# Revit family: 15_CMP_FD312_PB2A
name_source: partatom
category: Porte
units: mm (PartAtom-declared; Revit-internal decimal feet)

## family parameters
Condiviso = No
Host = Muro
Numero OmniClass = 23.30.10.00
Punto di calcolo locali = Sì
Sempre verticale = Sì
Taglio con vuoti quando caricato = No
Titolo OmniClass = Doors

## types (3) — shared parameters
Altezza = 2100 mm
Chiusura muro = Per host
Codice assieme = B2030100
Costruzione analitica = <Nessuno>
EXTERNAL ALUMINUM FRAME/TELAIO ALLUMINIO ESTERNO = UNIFORM_ALUMINUM
Funzione = Interno
H = 2100 mm
HANDLE HEIGHT/ALTEZZA MANIGLIA = 1100 mm  [stored 3.60892 ft]
HANDLE/MANIGLIA = UNIFORM_ALUMINUM
HOLE_H = 2100 mm
HTI = 2085 mm  [stored 6.84055 ft]
INTERIOR WOOD FRAME/TELAIO LEGNO INTERNO = UNIFORM_WOOD
Immagine tipo = <Nessuno>
Larghezza telaio = 75 mm  [stored 0.246063 ft]
MAXIMUM WIDTH/LARGHEZZA MASSIMA = 1800 mm  [stored 5.90551 ft]
MAX_DIMENSIONS_WARNING = No
MINIMUM HEIGHT/ALTEZZA MINIMA = 1800 mm  [stored 5.90551 ft]
MINIMUM WIDTH/LARGHEZZA MINIMA  = 900 mm  [stored 2.95276 ft]
Modello = COMPLANARE
PRODUCER WEBSITE/SITO WEB PRODUTTORE = www.uniform.it
PRODUCT WEBSITE/SITO WEB PRODOTTO = www.sistema-uni-one.it
Produttore = UNIFORM
Proiezione telaio est. = 25 mm  [stored 0.082021 ft]
Proiezione telaio int. = 25 mm  [stored 0.082021 ft]
URL = https://www.sistema-uni-one.it
WINDOW GLASS/VETRO FINESTRA = UNIFORM_GLASS
zero-valued in all types: T_F_H, WINDOW HOLE TOLERANCE/TOLLERANZA FORO FINESTRA

## per-type parameters (varying)
| type | GLASS WEIGHT/PESO VETRO | HOLE_W | Larghezza | MAXIMUM HEIGHT/ALTEZZA MASSIMA | Rw GLASS/Rw VETRO | Rw WINDOW/Rw FINESTRA | Ug GLASS/Ug VETRO | Uw WINDOW/Uw FINESTRA | W | W/2 | W/2 APR |
| PB2A_ACOUSTICS | 60.00 kg/m² | 1800 mm  [stored 5.90551 ft] | 1800 mm  [stored 5.90551 ft] | 2400 mm | 49 | 43 | 1.1000 W/(m²·K) | 1.3000 W/(m²·K) | 1800 mm  [stored 5.90551 ft] | 932 mm | 931 mm  [stored 3.05446 ft] |
| PB2A_THERMAL | 43.00 kg/m² | 1000 mm  [stored 3.28084 ft] | 1000 mm  [stored 3.28084 ft] | 2500 mm  [stored 8.2021 ft] | 0 | 0 | 1.0000 W/(m²·K) | 1.2000 W/(m²·K) | 1000 mm  [stored 3.28084 ft] | 532 mm  [stored 1.74541 ft] | 531 mm  [stored 1.74213 ft] |
| PB2A_HIGH THERMAL PERFORMANCE | 43.00 kg/m² | 1000 mm  [stored 3.28084 ft] | 1000 mm  [stored 3.28084 ft] | 2500 mm  [stored 8.2021 ft] | 0 | 0 | 0.5000 W/(m²·K) | 0.8000 W/(m²·K) | 1000 mm  [stored 3.28084 ft] | 532 mm  [stored 1.74541 ft] | 531 mm  [stored 1.74213 ft] |

note: [stored X ft] marks values corroborated as IEEE doubles in the binary element streams (Revit-internal decimal feet)
